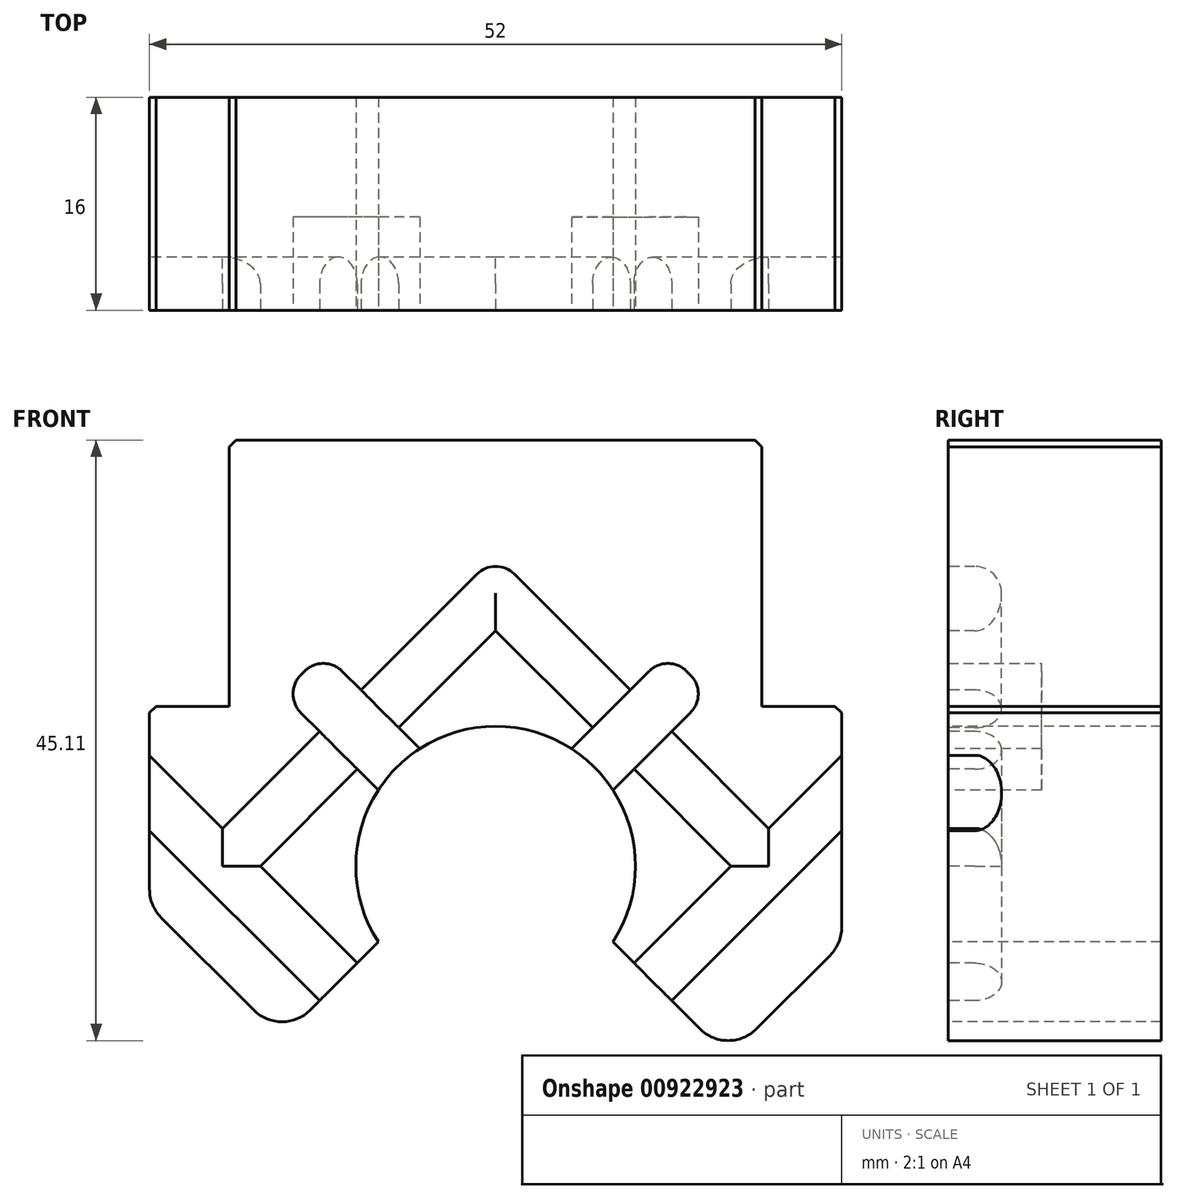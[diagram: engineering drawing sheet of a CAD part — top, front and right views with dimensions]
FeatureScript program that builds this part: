
annotation { "Feature Type Name" : "Feature", "Feature Type Description" : "" }
export const myFeature = defineFeature(function(context is Context, id is Id, definition is map)
    precondition{}
    {
        {
            var Q0;
            Q0=qCreatedBy(makeId("Front.planeOp"),FACE);
            var sketch = newSketch(context, id + "F0", { "sketchPlane" : qUnion([Q0])});
            skLineSegment(sketch, "E0", {"start": v(-23.46, -23.46) * mm, "end": v(26.19, 26.19) * mm, "construction": true});
            skLineSegment(sketch, "E1", {"start": v(-0.37, 20.88) * mm, "end": v(20.54, -0.03) * mm, "construction": true});
            skArc(sketch, "E2", {"start": v(8.82, -5.7) * mm, "mid": v(0, 10.5) * mm, "end": v(-8.82, -5.7) * mm});
            skLineSegment(sketch, "E3", {"start": v(0, -23.09) * mm, "end": v(0, 36.36) * mm, "construction": true});
            skLineSegment(sketch, "E4", {"start": v(-33.15, 0) * mm, "end": v(34.43, 0) * mm, "construction": true});
            skLineSegment(sketch, "E5", {"start": v(0, 32) * mm, "end": v(20, 32) * mm});
            skLineSegment(sketch, "E6", {"start": v(20, 32) * mm, "end": v(20, 12) * mm});
            skLineSegment(sketch, "E7", {"start": v(20, 12) * mm, "end": v(26, 12) * mm});
            skLineSegment(sketch, "E8", {"start": v(26, 12) * mm, "end": v(26, -5.82) * mm});
            skLineSegment(sketch, "E9.MirrorCS", {"start": v(0, 32) * mm, "end": v(-20, 32) * mm});
            skLineSegment(sketch, "E10.MirrorCS", {"start": v(-20, 32) * mm, "end": v(-20, 12) * mm});
            skLineSegment(sketch, "E11.MirrorCS", {"start": v(-20, 12) * mm, "end": v(-26, 12) * mm});
            skLineSegment(sketch, "E12.MirrorCS", {"start": v(-26, 12) * mm, "end": v(-26, -5.82) * mm});
            skLineSegment(sketch, "E13", {"start": v(5.7, 8.82) * mm, "end": v(12.94, 16.05) * mm});
            skLineSegment(sketch, "E14.MirrorCS", {"start": v(8.82, 5.7) * mm, "end": v(16.05, 12.94) * mm});
            skLineSegment(sketch, "E15", {"start": v(12.94, 16.05) * mm, "end": v(16.05, 12.94) * mm});
            skLineSegment(sketch, "E16", {"start": v(0, 17.68) * mm, "end": v(17.68, 0) * mm});
            skLineSegment(sketch, "E17", {"start": v(0, 23.33) * mm, "end": v(20.5, 2.83) * mm});
            skLineSegment(sketch, "E18.MirrorCS", {"start": v(-5.7, 8.82) * mm, "end": v(-12.94, 16.05) * mm});
            skLineSegment(sketch, "E19.MirrorCS", {"start": v(-8.82, 5.7) * mm, "end": v(-16.05, 12.94) * mm});
            skLineSegment(sketch, "E20.MirrorCS", {"start": v(-12.94, 16.05) * mm, "end": v(-16.05, 12.94) * mm});
            skLineSegment(sketch, "E21.MirrorCS", {"start": v(13.22, -10.11) * mm, "end": v(26, 2.67) * mm});
            skLineSegment(sketch, "E22.MirrorCS", {"start": v(10.4, -7.28) * mm, "end": v(17.68, 0) * mm});
            skLineSegment(sketch, "E23.MirrorCS", {"start": v(-8.82, -5.7) * mm, "end": v(-16.05, -12.94) * mm});
            skLineSegment(sketch, "E24.trimOffspring", {"start": v(20.5, 2.83) * mm, "end": v(26, 8.32) * mm});
            skLineSegment(sketch, "E25.MirrorCS", {"start": v(-13.22, -10.11) * mm, "end": v(-26, 2.67) * mm});
            skLineSegment(sketch, "E26.MirrorCS", {"start": v(-10.4, -7.28) * mm, "end": v(-17.68, 0) * mm});
            skLineSegment(sketch, "E27.MirrorCS", {"start": v(0, 17.68) * mm, "end": v(-17.68, 0) * mm});
            skLineSegment(sketch, "E28.MirrorCS", {"start": v(0, 23.33) * mm, "end": v(-20.5, 2.83) * mm});
            skLineSegment(sketch, "E29.MirrorCS", {"start": v(-20.5, 2.83) * mm, "end": v(-26, 8.32) * mm});
            skLineSegment(sketch, "E30.MirrorCS", {"start": v(-16.05, -12.94) * mm, "end": v(-26, -3) * mm});
            skLineSegment(sketch, "E31", {"start": v(8.82, -5.7) * mm, "end": v(17.47, -14.35) * mm});
            skLineSegment(sketch, "E32", {"start": v(17.47, -14.35) * mm, "end": v(26, -5.82) * mm});
            skSolve(sketch);
        }
        {
            var Q0;
            {var subQ1=sQuery(id+"F0.wireOp",EDGE,"E2");var subQ7=sQuery(id+"F0.wireOp",EDGE,"E13");var subQ9=makeQuery(id+"F0.imprint","INTERSECT",VERTEX,{"derivedFrom":[subQ1,subQ7]});Q0=makeQuery(id+"F0.imprint","IMPRINT",FACE,{"disambiguationData":[TD([[makeQuery(id+"F0.imprint","IMPRINT",EDGE,{"disambiguationData":[TD([[subQ9,-1.0]])],"derivedFrom":subQ1}),-1.0]])]});}
            var Q1;
            {var subQ0=sQuery(id+"F0.wireOp",EDGE,"E18.MirrorCS");var subQ1=sQuery(id+"F0.wireOp",EDGE,"E2");var subQ2=makeQuery(id+"F0.imprint","INTERSECT",VERTEX,{"derivedFrom":[subQ1,subQ0]});Q1=makeQuery(id+"F0.imprint","IMPRINT",FACE,{"disambiguationData":[TD([[makeQuery(id+"F0.imprint","IMPRINT",EDGE,{"disambiguationData":[TD([[subQ2,-1.0]])],"derivedFrom":subQ1}),-1.0]])]});}
            var Q2;
            {var subQ3=sQuery(id+"F0.wireOp",EDGE,"E26.MirrorCS");Q2=makeQuery(id+"F0.imprint","IMPRINT",FACE,{"disambiguationData":[TD([[makeQuery(id+"F0.imprint","IMPRINT",EDGE,{"derivedFrom":subQ3}),-1.0]])]});}
            var Q3;
            {var subQ0=sQuery(id+"F0.wireOp",EDGE,"E13");var subQ1=sQuery(id+"F0.wireOp",EDGE,"E2");var subQ2=makeQuery(id+"F0.imprint","INTERSECT",VERTEX,{"derivedFrom":[subQ1,subQ0]});Q3=makeQuery(id+"F0.imprint","IMPRINT",FACE,{"disambiguationData":[TD([[makeQuery(id+"F0.imprint","IMPRINT",EDGE,{"disambiguationData":[TD([[subQ2,1.0]])],"derivedFrom":subQ1}),-1.0]])]});}
            var Q4;
            {var subQ7=sQuery(id+"F0.wireOp",EDGE,"E13");var subQ9=sQuery(id+"F0.wireOp",EDGE,"E16");var subQ11=makeQuery(id+"F0.imprint","INTERSECT",VERTEX,{"derivedFrom":[subQ7,subQ9]});Q4=makeQuery(id+"F0.imprint","IMPRINT",FACE,{"disambiguationData":[TD([[makeQuery(id+"F0.imprint","IMPRINT",EDGE,{"disambiguationData":[TD([[subQ11,-1.0]])],"derivedFrom":subQ7}),1.0]])]});}
            var Q5;
            {var subQ0=sQuery(id+"F0.wireOp",EDGE,"E16");var subQ1=sQuery(id+"F0.wireOp",EDGE,"E13");var subQ2=makeQuery(id+"F0.imprint","INTERSECT",VERTEX,{"derivedFrom":[subQ1,subQ0]});Q5=makeQuery(id+"F0.imprint","IMPRINT",FACE,{"disambiguationData":[TD([[makeQuery(id+"F0.imprint","IMPRINT",EDGE,{"disambiguationData":[TD([[subQ2,-1.0]])],"derivedFrom":subQ1}),-1.0]])]});}
            var Q6;
            {var subQ0=sQuery(id+"F0.wireOp",EDGE,"E27.MirrorCS");var subQ1=sQuery(id+"F0.wireOp",EDGE,"E18.MirrorCS");var subQ2=makeQuery(id+"F0.imprint","INTERSECT",VERTEX,{"derivedFrom":[subQ1,subQ0]});Q6=makeQuery(id+"F0.imprint","IMPRINT",FACE,{"disambiguationData":[TD([[makeQuery(id+"F0.imprint","IMPRINT",EDGE,{"disambiguationData":[TD([[subQ2,-1.0]])],"derivedFrom":subQ1}),1.0]])]});}
            var Q7;
            {var subQ0=sQuery(id+"F0.wireOp",EDGE,"E25.MirrorCS");Q7=makeQuery(id+"F0.imprint","IMPRINT",FACE,{"disambiguationData":[TD([[makeQuery(id+"F0.imprint","IMPRINT",EDGE,{"derivedFrom":subQ0}),-1.0]])]});}
            var Q8;
            {var subQ0=sQuery(id+"F0.wireOp",EDGE,"E20.MirrorCS");Q8=makeQuery(id+"F0.imprint","IMPRINT",FACE,{"disambiguationData":[TD([[makeQuery(id+"F0.imprint","IMPRINT",EDGE,{"derivedFrom":subQ0}),1.0]])]});}
            var Q9;
            {var subQ0=sQuery(id+"F0.wireOp",EDGE,"E21.MirrorCS");Q9=makeQuery(id+"F0.imprint","IMPRINT",FACE,{"disambiguationData":[TD([[makeQuery(id+"F0.imprint","IMPRINT",EDGE,{"derivedFrom":subQ0}),1.0]])]});}
            var Q10;
            {var subQ0=sQuery(id+"F0.wireOp",EDGE,"E22.MirrorCS");Q10=makeQuery(id+"F0.imprint","IMPRINT",FACE,{"disambiguationData":[TD([[makeQuery(id+"F0.imprint","IMPRINT",EDGE,{"derivedFrom":subQ0}),1.0]])]});}
            var Q11;
            Q11=makeQuery(id+"F0.imprint","IMPRINT",FACE,{"disambiguationData":[TD([[makeQuery(id+"F0.imprint","IMPRINT",EDGE,{"derivedFrom":sQuery(id+"F0.wireOp",EDGE,"E5")}),-1.0]])]});
            var Q12;
            {var subQ0=sQuery(id+"F0.wireOp",EDGE,"E15");Q12=makeQuery(id+"F0.imprint","IMPRINT",FACE,{"disambiguationData":[TD([[makeQuery(id+"F0.imprint","IMPRINT",EDGE,{"derivedFrom":subQ0}),-1.0]])]});}
            var Q13;
            {var subQ2=sQuery(id+"F0.wireOp",EDGE,"E21.MirrorCS");Q13=makeQuery(id+"F0.imprint","IMPRINT",FACE,{"disambiguationData":[TD([[makeQuery(id+"F0.imprint","IMPRINT",EDGE,{"derivedFrom":subQ2}),-1.0]])]});}
            var Q14;
            {var subQ2=sQuery(id+"F0.wireOp",EDGE,"E25.MirrorCS");Q14=makeQuery(id+"F0.imprint","IMPRINT",FACE,{"disambiguationData":[TD([[makeQuery(id+"F0.imprint","IMPRINT",EDGE,{"derivedFrom":subQ2}),1.0]])]});}
            extrude(context, id + "F1", {"entities" : qUnion([Q0, Q1, Q2, Q3, Q4, Q5, Q6, Q7, Q8, Q9, Q10, Q11, Q12, Q13, Q14]), "oppositeDirection" : true, "depth" : 16 * mm, "offsetDistance" : 25 * mm});
        }
        {
            var Q0;
            {var subQ0=sQuery(id+"F0.wireOp",EDGE,"E15");Q0=makeQuery(id+"F0.imprint","IMPRINT",FACE,{"disambiguationData":[TD([[makeQuery(id+"F0.imprint","IMPRINT",EDGE,{"derivedFrom":subQ0}),-1.0]])]});}
            var Q1;
            {var subQ0=sQuery(id+"F0.wireOp",EDGE,"E16");var subQ1=sQuery(id+"F0.wireOp",EDGE,"E13");var subQ2=makeQuery(id+"F0.imprint","INTERSECT",VERTEX,{"derivedFrom":[subQ1,subQ0]});Q1=makeQuery(id+"F0.imprint","IMPRINT",FACE,{"disambiguationData":[TD([[makeQuery(id+"F0.imprint","IMPRINT",EDGE,{"disambiguationData":[TD([[subQ2,-1.0]])],"derivedFrom":subQ1}),-1.0]])]});}
            var Q2;
            {var subQ0=sQuery(id+"F0.wireOp",EDGE,"E13");var subQ1=sQuery(id+"F0.wireOp",EDGE,"E2");var subQ2=makeQuery(id+"F0.imprint","INTERSECT",VERTEX,{"derivedFrom":[subQ1,subQ0]});Q2=makeQuery(id+"F0.imprint","IMPRINT",FACE,{"disambiguationData":[TD([[makeQuery(id+"F0.imprint","IMPRINT",EDGE,{"disambiguationData":[TD([[subQ2,1.0]])],"derivedFrom":subQ1}),-1.0]])]});}
            var Q3;
            {var subQ0=sQuery(id+"F0.wireOp",EDGE,"E18.MirrorCS");var subQ1=sQuery(id+"F0.wireOp",EDGE,"E2");var subQ2=makeQuery(id+"F0.imprint","INTERSECT",VERTEX,{"derivedFrom":[subQ1,subQ0]});Q3=makeQuery(id+"F0.imprint","IMPRINT",FACE,{"disambiguationData":[TD([[makeQuery(id+"F0.imprint","IMPRINT",EDGE,{"disambiguationData":[TD([[subQ2,-1.0]])],"derivedFrom":subQ1}),-1.0]])]});}
            var Q4;
            {var subQ5=sQuery(id+"F0.wireOp",EDGE,"E20.MirrorCS");Q4=makeQuery(id+"F0.imprint","IMPRINT",FACE,{"disambiguationData":[TD([[makeQuery(id+"F0.imprint","IMPRINT",EDGE,{"derivedFrom":subQ5}),1.0]])]});}
            var Q5;
            {var subQ0=sQuery(id+"F0.wireOp",EDGE,"E27.MirrorCS");var subQ1=sQuery(id+"F0.wireOp",EDGE,"E18.MirrorCS");var subQ2=makeQuery(id+"F0.imprint","INTERSECT",VERTEX,{"derivedFrom":[subQ1,subQ0]});Q5=makeQuery(id+"F0.imprint","IMPRINT",FACE,{"disambiguationData":[TD([[makeQuery(id+"F0.imprint","IMPRINT",EDGE,{"disambiguationData":[TD([[subQ2,-1.0]])],"derivedFrom":subQ1}),1.0]])]});}
            extrude(context, id + "F2", {"entities" : qUnion([Q0, Q1, Q2, Q3, Q4, Q5]), "operationType" : NewBodyOperationType.REMOVE, "oppositeDirection" : true, "depth" : 7 * mm, "offsetDistance" : 25 * mm});
        }
        {
            var Q0;
            {var subQ1=sQuery(id+"F0.wireOp",EDGE,"E16");var subQ8=sQuery(id+"F0.wireOp",EDGE,"E13");var subQ10=makeQuery(id+"F0.imprint","INTERSECT",VERTEX,{"derivedFrom":[subQ8,subQ1]});Q0=makeQuery(id+"F0.imprint","IMPRINT",FACE,{"disambiguationData":[TD([[makeQuery(id+"F0.imprint","IMPRINT",EDGE,{"disambiguationData":[TD([[subQ10,-1.0]])],"derivedFrom":subQ8}),1.0]])]});}
            var Q1;
            {var subQ0=sQuery(id+"F0.wireOp",EDGE,"E21.MirrorCS");Q1=makeQuery(id+"F0.imprint","IMPRINT",FACE,{"disambiguationData":[TD([[makeQuery(id+"F0.imprint","IMPRINT",EDGE,{"derivedFrom":subQ0}),1.0]])]});}
            var Q2;
            {var subQ0=sQuery(id+"F0.wireOp",EDGE,"E25.MirrorCS");Q2=makeQuery(id+"F0.imprint","IMPRINT",FACE,{"disambiguationData":[TD([[makeQuery(id+"F0.imprint","IMPRINT",EDGE,{"derivedFrom":subQ0}),-1.0]])]});}
            extrude(context, id + "F3", {"entities" : qUnion([Q0, Q1, Q2]), "operationType" : NewBodyOperationType.REMOVE, "oppositeDirection" : true, "depth" : 4 * mm, "offsetDistance" : 25 * mm});
        }
        {
            var Q0;
            Q0=makeQuery(id+"F2.boolean.opBoolean","COPY",EDGE,{"derivedFrom":makeQuery(id+"F2.opExtrude","SWEPT_EDGE",EDGE,{"disambiguationData":[OSD([sQuery(id+"F0.wireOp",EDGE,"E19.MirrorCS"),sQuery(id+"F0.wireOp",EDGE,"E20.MirrorCS")])]})});
            var Q1;
            Q1=makeQuery(id+"F2.boolean.opBoolean","COPY",EDGE,{"derivedFrom":makeQuery(id+"F2.opExtrude","SWEPT_EDGE",EDGE,{"disambiguationData":[OSD([sQuery(id+"F0.wireOp",EDGE,"E18.MirrorCS"),sQuery(id+"F0.wireOp",EDGE,"E20.MirrorCS")])]})});
            var Q2;
            Q2=makeQuery(id+"F2.boolean.opBoolean","COPY",EDGE,{"derivedFrom":makeQuery(id+"F2.opExtrude","SWEPT_EDGE",EDGE,{"disambiguationData":[OSD([sQuery(id+"F0.wireOp",EDGE,"E13"),sQuery(id+"F0.wireOp",EDGE,"E15")])]})});
            var Q3;
            Q3=makeQuery(id+"F2.boolean.opBoolean","COPY",EDGE,{"derivedFrom":makeQuery(id+"F2.opExtrude","SWEPT_EDGE",EDGE,{"disambiguationData":[OSD([sQuery(id+"F0.wireOp",EDGE,"E14.MirrorCS"),sQuery(id+"F0.wireOp",EDGE,"E15")])]})});
            var Q4;
            Q4=makeQuery(id+"F3.boolean.opBoolean","COPY",EDGE,{"derivedFrom":makeQuery(id+"F3.opExtrude","SWEPT_EDGE",EDGE,{"disambiguationData":[OSD([sQuery(id+"F0.wireOp",EDGE,"E17"),sQuery(id+"F0.wireOp",EDGE,"E28.MirrorCS")])]})});
            fillet(context, id + "F4", {"entities" : qUnion([Q0, Q1, Q2, Q3, Q4]), "radius" : 2 * mm, "tangentPropagation" : true, "allowEdgeOverflow" : false});
        }
        {
            var Q0;
            {var subQ0=sQuery(id+"F0.wireOp",EDGE,"E16");Q0=makeQuery(id+"F3.boolean.opBoolean","COPY",EDGE,{"derivedFrom":makeQuery(id+"F3.opExtrude","CAP_EDGE",EDGE,{"disambiguationData":[OSD([subQ0]),TDD([makeQuery(id+"F0.imprint","IMPRINT",EDGE,{"disambiguationData":[TD([[makeQuery(id+"F0.imprint","INTERSECT",VERTEX,{"derivedFrom":[subQ0,sQuery(id+"F0.wireOp",EDGE,"5782ae04-5cbb-4565-bf48-bf3dccf2a9680.MirrorCS")]}),-1.0]])],"derivedFrom":subQ0})])],"isStart":false})});}
            var Q1;
            Q1=makeQuery(id+"F3.boolean.opBoolean","COPY",EDGE,{"derivedFrom":makeQuery(id+"F3.opExtrude","CAP_EDGE",EDGE,{"disambiguationData":[OSD([sQuery(id+"F0.wireOp",EDGE,"E21.MirrorCS")])],"isStart":false})});
            var Q2;
            Q2=makeQuery(id+"F3.boolean.opBoolean","COPY",EDGE,{"derivedFrom":makeQuery(id+"F3.opExtrude","CAP_EDGE",EDGE,{"disambiguationData":[OSD([sQuery(id+"F0.wireOp",EDGE,"E22.MirrorCS")])],"isStart":false})});
            var Q3;
            {var subQ0=sQuery(id+"F0.wireOp",EDGE,"E16");Q3=makeQuery(id+"F3.boolean.opBoolean","COPY",EDGE,{"derivedFrom":makeQuery(id+"F3.opExtrude","CAP_EDGE",EDGE,{"disambiguationData":[OSD([subQ0]),TDD([makeQuery(id+"F0.imprint","IMPRINT",EDGE,{"disambiguationData":[TD([[makeQuery(id+"F0.imprint","INTERSECT",VERTEX,{"derivedFrom":[subQ0,sQuery(id+"F0.wireOp",EDGE,"E22.MirrorCS")]}),1.0]])],"derivedFrom":subQ0})])],"isStart":false})});}
            var Q4;
            {var subQ0=sQuery(id+"F0.wireOp",EDGE,"E17");Q4=makeQuery(id+"F3.boolean.opBoolean","COPY",EDGE,{"derivedFrom":makeQuery(id+"F3.opExtrude","CAP_EDGE",EDGE,{"disambiguationData":[OSD([subQ0]),TDD([makeQuery(id+"F0.imprint","IMPRINT",EDGE,{"disambiguationData":[TD([[makeQuery(id+"F0.imprint","INTERSECT",VERTEX,{"derivedFrom":[subQ0,sQuery(id+"F0.wireOp",EDGE,"E24.trimOffspring")]}),1.0]])],"derivedFrom":subQ0})])],"isStart":false})});}
            var Q5;
            {var subQ0=sQuery(id+"F0.wireOp",EDGE,"E17");Q5=makeQuery(id+"F3.boolean.opBoolean","COPY",EDGE,{"derivedFrom":makeQuery(id+"F3.opExtrude","CAP_EDGE",EDGE,{"disambiguationData":[OSD([subQ0]),TDD([makeQuery(id+"F0.imprint","IMPRINT",EDGE,{"disambiguationData":[TD([[makeQuery(id+"F0.imprint","INTERSECT",VERTEX,{"derivedFrom":[subQ0,sQuery(id+"F0.wireOp",EDGE,"E28.MirrorCS")]}),-1.0]])],"derivedFrom":subQ0})])],"isStart":false})});}
            var Q6;
            {var subQ0=sQuery(id+"F0.wireOp",EDGE,"E28.MirrorCS");Q6=makeQuery(id+"F3.boolean.opBoolean","COPY",EDGE,{"derivedFrom":makeQuery(id+"F3.opExtrude","CAP_EDGE",EDGE,{"disambiguationData":[OSD([subQ0]),TDD([makeQuery(id+"F0.imprint","IMPRINT",EDGE,{"disambiguationData":[TD([[makeQuery(id+"F0.imprint","INTERSECT",VERTEX,{"derivedFrom":[subQ0,sQuery(id+"F0.wireOp",EDGE,"E29.MirrorCS")]}),1.0]])],"derivedFrom":subQ0})])],"isStart":false})});}
            var Q7;
            Q7=makeQuery(id+"F3.boolean.opBoolean","COPY",EDGE,{"derivedFrom":makeQuery(id+"F3.opExtrude","CAP_EDGE",EDGE,{"disambiguationData":[OSD([sQuery(id+"F0.wireOp",EDGE,"E29.MirrorCS")])],"isStart":false})});
            var Q8;
            Q8=makeQuery(id+"F3.boolean.opBoolean","COPY",EDGE,{"derivedFrom":makeQuery(id+"F3.opExtrude","CAP_EDGE",EDGE,{"disambiguationData":[OSD([sQuery(id+"F0.wireOp",EDGE,"E26.MirrorCS")])],"isStart":false})});
            var Q9;
            {var subQ0=sQuery(id+"F0.wireOp",EDGE,"E27.MirrorCS");Q9=makeQuery(id+"F3.boolean.opBoolean","COPY",EDGE,{"derivedFrom":makeQuery(id+"F3.opExtrude","CAP_EDGE",EDGE,{"disambiguationData":[OSD([subQ0]),TDD([makeQuery(id+"F0.imprint","IMPRINT",EDGE,{"disambiguationData":[TD([[makeQuery(id+"F0.imprint","INTERSECT",VERTEX,{"derivedFrom":[sQuery(id+"F0.wireOp",EDGE,"E16"),subQ0]}),-1.0]])],"derivedFrom":subQ0})])],"isStart":false})});}
            var Q10;
            {var subQ0=sQuery(id+"F0.wireOp",EDGE,"E27.MirrorCS");Q10=makeQuery(id+"F3.boolean.opBoolean","COPY",EDGE,{"derivedFrom":makeQuery(id+"F3.opExtrude","CAP_EDGE",EDGE,{"disambiguationData":[OSD([subQ0]),TDD([makeQuery(id+"F0.imprint","IMPRINT",EDGE,{"disambiguationData":[TD([[makeQuery(id+"F0.imprint","INTERSECT",VERTEX,{"derivedFrom":[sQuery(id+"F0.wireOp",EDGE,"E26.MirrorCS"),subQ0]}),1.0]])],"derivedFrom":subQ0})])],"isStart":false})});}
            var Q11;
            Q11=makeQuery(id+"F3.boolean.opBoolean","COPY",EDGE,{"derivedFrom":makeQuery(id+"F3.opExtrude","CAP_EDGE",EDGE,{"disambiguationData":[OSD([sQuery(id+"F0.wireOp",EDGE,"E25.MirrorCS")])],"isStart":false})});
            var Q12;
            Q12=makeQuery(id+"F3.boolean.opBoolean","COPY",EDGE,{"derivedFrom":makeQuery(id+"F3.opExtrude","CAP_EDGE",EDGE,{"disambiguationData":[OSD([sQuery(id+"F0.wireOp",EDGE,"E24.trimOffspring")])],"isStart":false})});
            fillet(context, id + "F5", {"entities" : qUnion([Q0, Q1, Q2, Q3, Q4, Q5, Q6, Q7, Q8, Q9, Q10, Q11, Q12]), "radius" : 2 * mm, "tangentPropagation" : true, "allowEdgeOverflow" : false});
        }
        {
            var Q0;
            Q0=makeQuery(id+"F1.opExtrude","SWEPT_EDGE",EDGE,{"disambiguationData":[OSD([sQuery(id+"F0.wireOp",EDGE,"E31"),sQuery(id+"F0.wireOp",EDGE,"E32")])]});
            var Q1;
            Q1=makeQuery(id+"F1.opExtrude","SWEPT_EDGE",EDGE,{"disambiguationData":[OSD([sQuery(id+"F0.wireOp",EDGE,"E23.MirrorCS"),sQuery(id+"F0.wireOp",EDGE,"E30.MirrorCS")])]});
            var Q2;
            Q2=makeQuery(id+"F1.opExtrude","SWEPT_EDGE",EDGE,{"disambiguationData":[OSD([sQuery(id+"F0.wireOp",EDGE,"E8"),sQuery(id+"F0.wireOp",EDGE,"E32")])]});
            var Q3;
            Q3=makeQuery(id+"F1.opExtrude","SWEPT_EDGE",EDGE,{"disambiguationData":[OSD([sQuery(id+"F0.wireOp",EDGE,"E12.MirrorCS"),sQuery(id+"F0.wireOp",EDGE,"E30.MirrorCS")])]});
            fillet(context, id + "F6", {"entities" : qUnion([Q0, Q1, Q2, Q3]), "radius" : 3 * mm, "tangentPropagation" : true, "allowEdgeOverflow" : false});
        }
        {
            var Q0;
            Q0=makeQuery(id+"F1.opExtrude","SWEPT_EDGE",EDGE,{"disambiguationData":[OSD([sQuery(id+"F0.wireOp",EDGE,"E5"),sQuery(id+"F0.wireOp",EDGE,"E6")])]});
            var Q1;
            Q1=makeQuery(id+"F1.opExtrude","SWEPT_EDGE",EDGE,{"disambiguationData":[OSD([sQuery(id+"F0.wireOp",EDGE,"E7"),sQuery(id+"F0.wireOp",EDGE,"E8")])]});
            var Q2;
            Q2=makeQuery(id+"F1.opExtrude","SWEPT_EDGE",EDGE,{"disambiguationData":[OSD([sQuery(id+"F0.wireOp",EDGE,"E9.MirrorCS"),sQuery(id+"F0.wireOp",EDGE,"E10.MirrorCS")])]});
            var Q3;
            Q3=makeQuery(id+"F1.opExtrude","SWEPT_EDGE",EDGE,{"disambiguationData":[OSD([sQuery(id+"F0.wireOp",EDGE,"E11.MirrorCS"),sQuery(id+"F0.wireOp",EDGE,"E12.MirrorCS")])]});
            chamfer(context, id + "F7", {"entities" : qUnion([Q0, Q1, Q2, Q3]), "width" : 0.5 * mm, "tangentPropagation" : true});
        }
    });
